# Revit family: AFX-Leia-LED_Vanity-1
name_source: partatom
category: Lighting Fixtures
units: mm (PartAtom-declared; Revit-internal decimal feet)

## family parameters
Cut with Voids When Loaded = No
Host = Face
Light Source = Yes
Part Type = Normal
Room Calculation Point = No
Round Connector Dimension = Use Diameter
Shared = No

## types (3) — shared parameters
Apparent Load = 0 VA
Assembly Code = D5020200
Body Finish = AFX - Paint Finish Black
Color Filter = 16777215
Colour Rendering Index = 90
Default Elevation = 48"
Depth = 4"
Diffuser Finish = AFX - Acrylic
Dimming Lamp Color Temperature Shift = <None>
Emit Shape Visible in Rendering = No
Emit from Rectangle Length = 1 3/4"
Height = 4 1/2"
Housing Finish = AFX - Paint Finish Black
Keynote = 12500
Manufacturer = AFX Inc
Power Factor = 1
Product Documentation Link = https://www.afxinc.com
Revit Model Built By = https://www.servex-us.com
Sustainability = https://lamprecycle.org
Tilt Angle = 90.00°
Type Comments = Leia
URL = https://www.afxinc.com
Voltage = 120 V

## per-type parameters (varying)
| type | Description | Emit from Rectangle Width | Length | Photometric Web File | Wattage Comments |
| LIAV2404LAJUDBK | LED Vanity - Universal Driver  - 24 3/4"L x 4 1/2"H x 4"D | 24" | 24 3/4" | LIAV2404LAJUDBK_3000K_IES.IES | 18w |
| LIAV3604LAJUDBK | LED Vanity - Universal Driver  - 36 3/4"L x 4 1/2"H x 4"D | 36" | 36 3/4" | LIAV3604LAJUDBK_3000K_IES.IES | 26w |
| LIAV4804LAJUDBK | LED Vanity - Universal Driver  - 48"L x 4 1/2"H x 4"D | 47 1/4" | 48" | LIAV4804LAJUDBK_3000K_IES.IES | 34w |

note: column(s) folded — value = type name in every type: Model

## geometry (parser evidence)
native form markers: Sweep x3
no freeform markers — native parametric forms only
